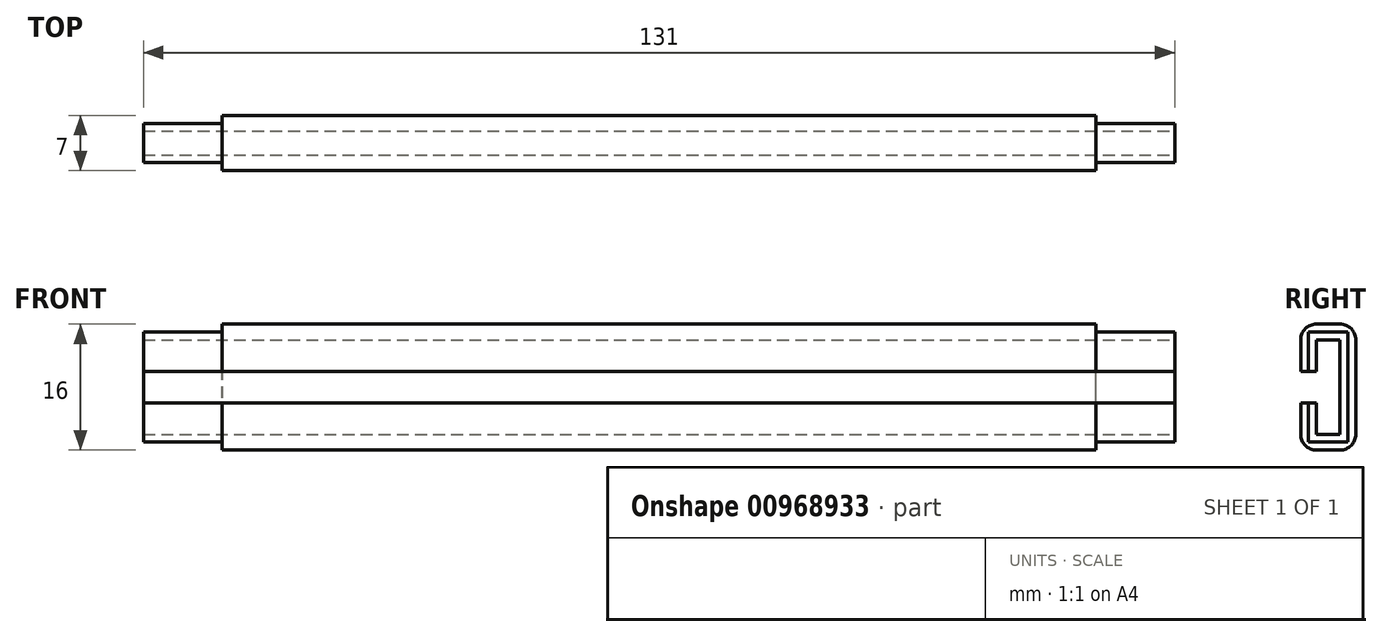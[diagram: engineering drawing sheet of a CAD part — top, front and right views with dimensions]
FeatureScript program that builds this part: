
annotation { "Feature Type Name" : "Feature", "Feature Type Description" : "" }
export const myFeature = defineFeature(function(context is Context, id is Id, definition is map)
    precondition{}
    {
        {
            var Q0;
            Q0=qCreatedBy(makeId("Front.planeOp"),FACE);
            var sketch = newSketch(context, id + "F0", { "sketchPlane" : qUnion([Q0])});
            skLineSegment(sketch, "E0.bottom", {"start": v(-19.62, 9.26) * mm, "end": v(101.38, 9.26) * mm});
            skLineSegment(sketch, "E0.top", {"start": v(-19.62, 25.26) * mm, "end": v(101.38, 25.26) * mm});
            skLineSegment(sketch, "E0.left", {"start": v(-19.62, 9.26) * mm, "end": v(-19.62, 25.26) * mm});
            skLineSegment(sketch, "E0.right", {"start": v(101.38, 9.26) * mm, "end": v(101.38, 25.26) * mm});
            skSolve(sketch);
        }
        {
            var Q0;
            Q0=makeQuery(id+"F0.imprint","IMPRINT",FACE,{"disambiguationData":[TD([[makeQuery(id+"F0.imprint","IMPRINT",EDGE,{"derivedFrom":sQuery(id+"F0.wireOp",EDGE,"E0.bottom")}),1.0]])]});
            extrude(context, id + "F1", {"entities" : qUnion([Q0]), "depth" : 7 * mm, "offsetDistance" : 25 * mm});
        }
        {
            var Q0;
            Q0=makeQuery(id+"F1.opExtrude","SWEPT_FACE",FACE,{"disambiguationData":[OSD([sQuery(id+"F0.wireOp",EDGE,"E0.right")])]});
            var sketch = newSketch(context, id + "F2", { "sketchPlane" : qUnion([Q0])});
            skLineSegment(sketch, "E1", {"start": v(-7, 15.26) * mm, "end": v(-5, 15.26) * mm});
            skLineSegment(sketch, "E2", {"start": v(-5, 15.26) * mm, "end": v(-5, 11.26) * mm});
            skLineSegment(sketch, "E3", {"start": v(-5, 11.26) * mm, "end": v(-2, 11.26) * mm});
            skLineSegment(sketch, "E4", {"start": v(-2, 11.26) * mm, "end": v(-2, 23.26) * mm});
            skLineSegment(sketch, "E5", {"start": v(-2, 23.26) * mm, "end": v(-5, 23.26) * mm});
            skLineSegment(sketch, "E6", {"start": v(-5, 23.26) * mm, "end": v(-5, 19.26) * mm});
            skLineSegment(sketch, "E7", {"start": v(-5, 19.26) * mm, "end": v(-7, 19.26) * mm});
            skLineSegment(sketch, "E8", {"start": v(-7, 19.26) * mm, "end": v(-7, 15.26) * mm});
            skSolve(sketch);
        }
        {
            var Q0;
            Q0=makeQuery(id+"F2.imprint","IMPRINT",FACE,{"disambiguationData":[TD([[makeQuery(id+"F2.imprint","IMPRINT",EDGE,{"derivedFrom":sQuery(id+"F2.wireOp",EDGE,"E1")}),1.0]])]});
            extrude(context, id + "F3", {"entities" : qUnion([Q0]), "operationType" : NewBodyOperationType.REMOVE, "endBound" : BoundingType.THROUGH_ALL, "oppositeDirection" : true, "depth" : 25 * mm, "offsetDistance" : 25 * mm});
        }
        {
            var Q0;
            Q0=makeQuery(id+"F1.opExtrude","SWEPT_FACE",FACE,{"disambiguationData":[OSD([sQuery(id+"F0.wireOp",EDGE,"E0.right")])]});
            var sketch = newSketch(context, id + "F4", { "sketchPlane" : qUnion([Q0])});
            skLineSegment(sketch, "E9.bottom", {"start": v(-6, 10.26) * mm, "end": v(-1, 10.26) * mm});
            skLineSegment(sketch, "E9.top", {"start": v(-6, 24.26) * mm, "end": v(-1, 24.26) * mm});
            skLineSegment(sketch, "E9.left", {"start": v(-6, 10.26) * mm, "end": v(-6, 24.26) * mm});
            skLineSegment(sketch, "E9.right", {"start": v(-1, 10.26) * mm, "end": v(-1, 24.26) * mm});
            skSolve(sketch);
        }
        {
            var Q0;
            {var subQ1=sQuery(id+"F4.wireOp",EDGE,"E9.bottom");Q0=makeQuery(id+"F4.imprint","IMPRINT",FACE,{"disambiguationData":[TD([[makeQuery(id+"F4.imprint","IMPRINT",EDGE,{"derivedFrom":subQ1}),1.0]])]});}
            extrude(context, id + "F5", {"entities" : qUnion([Q0]), "operationType" : NewBodyOperationType.ADD, "depth" : 10 * mm, "offsetDistance" : 25 * mm});
        }
        {
            var Q0;
            Q0=makeQuery(id+"F1.opExtrude","SWEPT_FACE",FACE,{"disambiguationData":[OSD([sQuery(id+"F0.wireOp",EDGE,"E0.left")])]});
            var sketch = newSketch(context, id + "F6", { "sketchPlane" : qUnion([Q0])});
            skLineSegment(sketch, "E10.bottom", {"start": v(6, 24.26) * mm, "end": v(1, 24.26) * mm});
            skLineSegment(sketch, "E10.top", {"start": v(6, 10.26) * mm, "end": v(1, 10.26) * mm});
            skLineSegment(sketch, "E10.left", {"start": v(6, 24.26) * mm, "end": v(6, 10.26) * mm});
            skLineSegment(sketch, "E10.right", {"start": v(1, 24.26) * mm, "end": v(1, 10.26) * mm});
            skSolve(sketch);
        }
        {
            var Q0;
            {var subQ8=sQuery(id+"F6.wireOp",EDGE,"E10.bottom");Q0=makeQuery(id+"F6.imprint","IMPRINT",FACE,{"disambiguationData":[TD([[makeQuery(id+"F6.imprint","IMPRINT",EDGE,{"derivedFrom":subQ8}),-1.0]])]});}
            extrude(context, id + "F7", {"entities" : qUnion([Q0]), "operationType" : NewBodyOperationType.REMOVE, "oppositeDirection" : true, "depth" : 10 * mm, "offsetDistance" : 25 * mm});
        }
        {
            var Q0;
            Q0=makeQuery(id+"F1.opExtrude","CAP_EDGE",EDGE,{"disambiguationData":[OSD([sQuery(id+"F0.wireOp",EDGE,"E0.top")])],"isStart":false});
            var Q1;
            Q1=makeQuery(id+"F1.opExtrude","CAP_EDGE",EDGE,{"disambiguationData":[OSD([sQuery(id+"F0.wireOp",EDGE,"E0.bottom")])],"isStart":false});
            var Q2;
            Q2=makeQuery(id+"F1.opExtrude","CAP_EDGE",EDGE,{"disambiguationData":[OSD([sQuery(id+"F0.wireOp",EDGE,"E0.top")])],"isStart":true});
            var Q3;
            Q3=makeQuery(id+"F1.opExtrude","CAP_EDGE",EDGE,{"disambiguationData":[OSD([sQuery(id+"F0.wireOp",EDGE,"E0.bottom")])],"isStart":true});
            fillet(context, id + "F8", {"entities" : qUnion([Q0, Q1, Q2, Q3]), "radius" : 2 * mm, "tangentPropagation" : true, "allowEdgeOverflow" : false});
        }
    });
